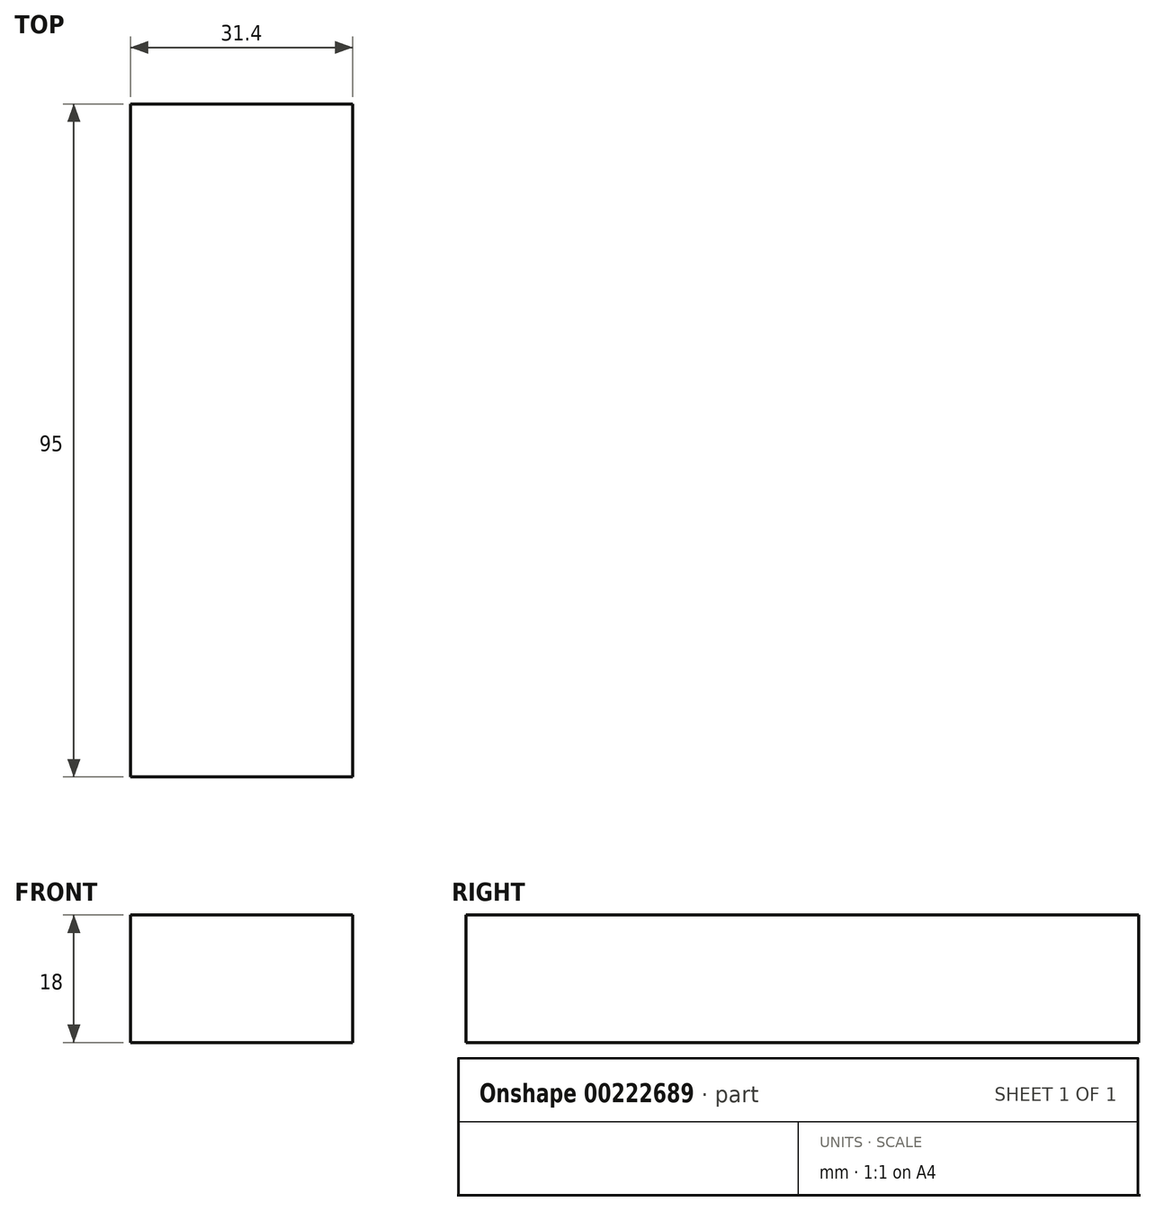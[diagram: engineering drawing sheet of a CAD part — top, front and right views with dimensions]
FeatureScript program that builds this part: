
annotation { "Feature Type Name" : "Feature", "Feature Type Description" : "" }
export const myFeature = defineFeature(function(context is Context, id is Id, definition is map)
    precondition{}
    {
        {
            var Q0;
            Q0=qCreatedBy(makeId("Top.planeOp"),FACE);
            var sketch = newSketch(context, id + "F0", { "sketchPlane" : qUnion([Q0])});
            skLineSegment(sketch, "E0.bottom", {"start": v(-6.12, 35.5) * mm, "end": v(25.28, 35.5) * mm});
            skLineSegment(sketch, "E0.top", {"start": v(-6.12, -59.5) * mm, "end": v(25.28, -59.5) * mm});
            skLineSegment(sketch, "E0.left", {"start": v(-6.12, 35.5) * mm, "end": v(-6.12, -59.5) * mm});
            skLineSegment(sketch, "E0.right", {"start": v(25.28, 35.5) * mm, "end": v(25.28, -59.5) * mm});
            skSolve(sketch);
        }
        {
            var Q0;
            Q0=makeQuery(id+"F0.imprint","IMPRINT",FACE,{"disambiguationData":[TD([[makeQuery(id+"F0.imprint","IMPRINT",EDGE,{"derivedFrom":sQuery(id+"F0.wireOp",EDGE,"E0.bottom")}),-1.0]])]});
            extrude(context, id + "F1", {"entities" : qUnion([Q0]), "depth" : 18 * mm});
        }
    });
